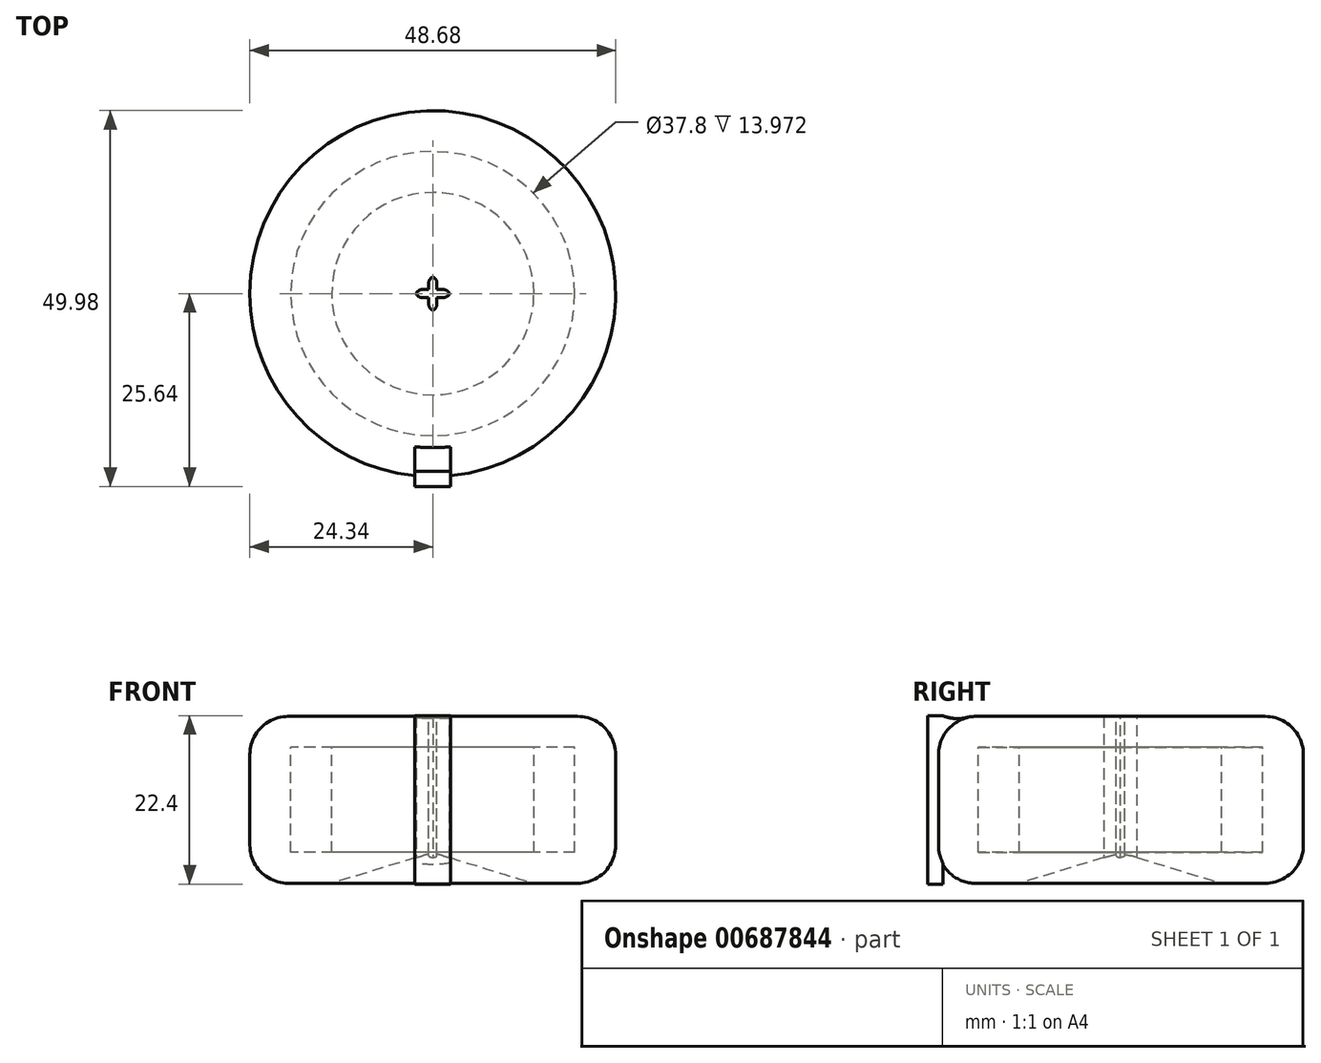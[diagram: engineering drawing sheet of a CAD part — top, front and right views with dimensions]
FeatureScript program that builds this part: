
annotation { "Feature Type Name" : "Feature", "Feature Type Description" : "" }
export const myFeature = defineFeature(function(context is Context, id is Id, definition is map)
    precondition{}
    {
        {
            var Q0;
            Q0=qCreatedBy(makeId("Front.planeOp"),FACE);
            var sketch = newSketch(context, id + "F0", { "sketchPlane" : qUnion([Q0])});
            skLineSegment(sketch, "E0.bottom", {"start": v(0, -6.99) * mm, "end": v(-18.9, -6.99) * mm});
            skLineSegment(sketch, "E0.top", {"start": v(0, 6.99) * mm, "end": v(-18.9, 6.99) * mm});
            skLineSegment(sketch, "E0.right", {"start": v(-18.9, -6.99) * mm, "end": v(-18.9, 6.99) * mm});
            skPoint(sketch, "E0.middle", {"position": v(0, 0) * mm});
            skLineSegment(sketch, "E1", {"start": v(0, 6.99) * mm, "end": v(0, -6.99) * mm});
            skPoint(sketch, "E0.left.end.orphan", {"position": v(18.9, 6.99) * mm});
            skPoint(sketch, "E2.orphan", {"position": v(18.9, -6.99) * mm});
            skLineSegment(sketch, "E3.bottom", {"start": v(-13.46, -11.1) * mm, "end": v(-24.34, -11.1) * mm});
            skLineSegment(sketch, "E3.top", {"start": v(-13.46, 11.1) * mm, "end": v(-24.34, 11.1) * mm});
            skLineSegment(sketch, "E3.left", {"start": v(-13.46, -11.1) * mm, "end": v(-13.46, 11.1) * mm});
            skLineSegment(sketch, "E3.right", {"start": v(-24.34, -11.1) * mm, "end": v(-24.34, 11.1) * mm});
            skPoint(sketch, "E3.middle", {"position": v(-18.9, 0) * mm});
            skLineSegment(sketch, "E4", {"start": v(0, -6.99) * mm, "end": v(-13.46, -11.1) * mm});
            skLineSegment(sketch, "E5", {"start": v(-13.46, 11.1) * mm, "end": v(0, 11.1) * mm});
            skLineSegment(sketch, "E6", {"start": v(0, 11.1) * mm, "end": v(0, 6.99) * mm});
            skSolve(sketch);
        }
        {
            var Q0;
            Q0 = qSketchRegion(id + "F0", true);
            var Q1;
            Q1=sQuery(id+"F0.wireOp",EDGE,"E1");
            revolve(context, id + "F1", {"entities" : qUnion([Q0]), "axis" : qUnion([Q1]), "revolveType" : RevolveType.FULL});
        }
        {
            var Q0;
            Q0=makeQuery(id+"F1.opRevolve","SWEPT_EDGE",EDGE,{"disambiguationData":[OSD([sQuery(id+"F0.wireOp",EDGE,"E3.top"),sQuery(id+"F0.wireOp",EDGE,"E3.right")])]});
            var Q1;
            Q1=makeQuery(id+"F1.opRevolve","SWEPT_EDGE",EDGE,{"disambiguationData":[OSD([sQuery(id+"F0.wireOp",EDGE,"E3.bottom"),sQuery(id+"F0.wireOp",EDGE,"E3.right")])]});
            fillet(context, id + "F2", {"entities" : qUnion([Q0, Q1]), "radius" : 5.08 * mm, "tangentPropagation" : true, "allowEdgeOverflow" : false});
        }
        {
            var Q0;
            Q0=qCreatedBy(makeId("Front.planeOp"),FACE);
            cPlane(context, id + "F3", {"entities" : qUnion([Q0]), "cplaneType" : CPlaneType.OFFSET, "offset" : 24.64 * mm, "width" : 152.4 * mm, "height" : 152.4 * mm});
        }
        {
            var Q0;
            Q0=qCreatedBy(id+"F3.planeOp",FACE);
            var sketch = newSketch(context, id + "F4", { "sketchPlane" : qUnion([Q0])});
            skLineSegment(sketch, "E7.bottom", {"start": v(2.38, -11.2) * mm, "end": v(-2.38, -11.2) * mm});
            skLineSegment(sketch, "E7.top", {"start": v(2.38, 11.2) * mm, "end": v(-2.38, 11.2) * mm});
            skLineSegment(sketch, "E7.left", {"start": v(2.38, -11.2) * mm, "end": v(2.38, 11.2) * mm});
            skLineSegment(sketch, "E7.right", {"start": v(-2.38, -11.2) * mm, "end": v(-2.38, 11.2) * mm});
            skPoint(sketch, "E7.middle", {"position": v(0, 0) * mm});
            skSolve(sketch);
        }
        {
            var Q0;
            Q0 = qSketchRegion(id + "F4", true);
            extrude(context, id + "F5", {"entities" : qUnion([Q0]), "operationType" : NewBodyOperationType.ADD, "endBound" : BoundingType.SYMMETRIC, "depth" : 2 * mm, "offsetDistance" : 25.4 * mm});
        }
        {
            var Q0;
            Q0=qCreatedBy(makeId("Top.planeOp"),FACE);
            cPlane(context, id + "F6", {"entities" : qUnion([Q0]), "cplaneType" : CPlaneType.OFFSET, "offset" : 11.68 * mm, "width" : 152.4 * mm, "height" : 152.4 * mm});
        }
        {
            var Q0;
            Q0=qCreatedBy(id+"F6.planeOp",FACE);
            var sketch = newSketch(context, id + "F7", { "sketchPlane" : qUnion([Q0])});
            skLineSegment(sketch, "E8.bottom", {"start": v(0.55, -2.34) * mm, "end": v(-0.55, -2.34) * mm});
            skLineSegment(sketch, "E8.top", {"start": v(0.55, 2.34) * mm, "end": v(-0.55, 2.34) * mm});
            skLineSegment(sketch, "E8.left", {"start": v(0.55, -2.34) * mm, "end": v(0.55, 2.34) * mm});
            skLineSegment(sketch, "E8.right", {"start": v(-0.55, -2.34) * mm, "end": v(-0.55, 2.34) * mm});
            skPoint(sketch, "E8.middle", {"position": v(0, 0) * mm});
            skLineSegment(sketch, "E9.bottom", {"start": v(2.34, -0.55) * mm, "end": v(-2.34, -0.55) * mm});
            skLineSegment(sketch, "E9.top", {"start": v(2.34, 0.55) * mm, "end": v(-2.34, 0.55) * mm});
            skLineSegment(sketch, "E9.left", {"start": v(2.34, -0.55) * mm, "end": v(2.34, 0.55) * mm});
            skLineSegment(sketch, "E9.right", {"start": v(-2.34, -0.55) * mm, "end": v(-2.34, 0.55) * mm});
            skSolve(sketch);
        }
        {
            var Q0;
            Q0 = qSketchRegion(id + "F7", true);
            extrude(context, id + "F8", {"entities" : qUnion([Q0]), "operationType" : NewBodyOperationType.REMOVE, "oppositeDirection" : true, "depth" : 25.4 * mm, "offsetDistance" : 25.4 * mm});
        }
        {
            var Q0;
            Q0=makeQuery(id+"F8.boolean.opBoolean","COPY",EDGE,{"derivedFrom":makeQuery(id+"F8.opExtrude","SWEPT_EDGE",EDGE,{"disambiguationData":[OSD([sQuery(id+"F7.wireOp",EDGE,"E9.bottom"),sQuery(id+"F7.wireOp",EDGE,"E9.right")])]})});
            var Q1;
            Q1=makeQuery(id+"F8.boolean.opBoolean","COPY",EDGE,{"derivedFrom":makeQuery(id+"F8.opExtrude","SWEPT_EDGE",EDGE,{"disambiguationData":[OSD([sQuery(id+"F7.wireOp",EDGE,"E9.top"),sQuery(id+"F7.wireOp",EDGE,"E9.right")])]})});
            var Q2;
            Q2=makeQuery(id+"F8.boolean.opBoolean","COPY",EDGE,{"derivedFrom":makeQuery(id+"F8.opExtrude","SWEPT_EDGE",EDGE,{"disambiguationData":[OSD([sQuery(id+"F7.wireOp",EDGE,"E8.top"),sQuery(id+"F7.wireOp",EDGE,"E8.right")])]})});
            var Q3;
            Q3=makeQuery(id+"F8.boolean.opBoolean","COPY",EDGE,{"derivedFrom":makeQuery(id+"F8.opExtrude","SWEPT_EDGE",EDGE,{"disambiguationData":[OSD([sQuery(id+"F7.wireOp",EDGE,"E8.top"),sQuery(id+"F7.wireOp",EDGE,"E8.left")])]})});
            var Q4;
            Q4=makeQuery(id+"F8.boolean.opBoolean","COPY",EDGE,{"derivedFrom":makeQuery(id+"F8.opExtrude","SWEPT_EDGE",EDGE,{"disambiguationData":[OSD([sQuery(id+"F7.wireOp",EDGE,"E8.bottom"),sQuery(id+"F7.wireOp",EDGE,"E8.right")])]})});
            var Q5;
            Q5=makeQuery(id+"F8.boolean.opBoolean","COPY",EDGE,{"derivedFrom":makeQuery(id+"F8.opExtrude","SWEPT_EDGE",EDGE,{"disambiguationData":[OSD([sQuery(id+"F7.wireOp",EDGE,"E8.bottom"),sQuery(id+"F7.wireOp",EDGE,"E8.left")])]})});
            var Q6;
            Q6=makeQuery(id+"F8.boolean.opBoolean","COPY",EDGE,{"derivedFrom":makeQuery(id+"F8.opExtrude","SWEPT_EDGE",EDGE,{"disambiguationData":[OSD([sQuery(id+"F7.wireOp",EDGE,"E9.bottom"),sQuery(id+"F7.wireOp",EDGE,"E9.left")])]})});
            var Q7;
            Q7=makeQuery(id+"F8.boolean.opBoolean","COPY",EDGE,{"derivedFrom":makeQuery(id+"F8.opExtrude","SWEPT_EDGE",EDGE,{"disambiguationData":[OSD([sQuery(id+"F7.wireOp",EDGE,"E9.top"),sQuery(id+"F7.wireOp",EDGE,"E9.left")])]})});
            fillet(context, id + "F9", {"entities" : qUnion([Q0, Q1, Q2, Q3, Q4, Q5, Q6, Q7]), "radius" : 1 * mm, "tangentPropagation" : true, "allowEdgeOverflow" : false});
        }
        {
            var Q0;
            Q0=makeQuery(id+"FWEGzIRy7pSOTiT_1.2.F5.boolean.opBoolean","INTERSECT",EDGE,{"derivedFrom":[makeQuery(id+"F2.opFillet","BLEND_FACE",FACE,{"disambiguationData":[OSD([sQuery(id+"F0.wireOp",EDGE,"E3.top"),sQuery(id+"F0.wireOp",EDGE,"E3.right")])]}),makeQuery(id+"FWEGzIRy7pSOTiT_1.2.F5.opExtrude","CAP_FACE",FACE,{"disambiguationData":[OSD([sQuery(id+"F4.wireOp",EDGE,"E7.bottom"),sQuery(id+"F4.wireOp",EDGE,"E7.top"),sQuery(id+"F4.wireOp",EDGE,"E7.left"),sQuery(id+"F4.wireOp",EDGE,"E7.right")])],"isStart":true})]});
            var Q1;
            Q1=makeQuery(id+"FWEGzIRy7pSOTiT_1.1.F5.boolean.opBoolean","INTERSECT",EDGE,{"derivedFrom":[makeQuery(id+"F2.opFillet","BLEND_FACE",FACE,{"disambiguationData":[OSD([sQuery(id+"F0.wireOp",EDGE,"E3.top"),sQuery(id+"F0.wireOp",EDGE,"E3.right")])]}),makeQuery(id+"FWEGzIRy7pSOTiT_1.1.F5.opExtrude","CAP_FACE",FACE,{"disambiguationData":[OSD([sQuery(id+"F4.wireOp",EDGE,"E7.bottom"),sQuery(id+"F4.wireOp",EDGE,"E7.top"),sQuery(id+"F4.wireOp",EDGE,"E7.left"),sQuery(id+"F4.wireOp",EDGE,"E7.right")])],"isStart":true})]});
            var Q2;
            Q2=makeQuery(id+"F5.boolean.opBoolean","INTERSECT",EDGE,{"derivedFrom":[makeQuery(id+"F2.opFillet","BLEND_FACE",FACE,{"disambiguationData":[OSD([sQuery(id+"F0.wireOp",EDGE,"E3.top"),sQuery(id+"F0.wireOp",EDGE,"E3.right")])]}),makeQuery(id+"F5.opExtrude","CAP_FACE",FACE,{"disambiguationData":[OSD([sQuery(id+"F4.wireOp",EDGE,"E7.bottom"),sQuery(id+"F4.wireOp",EDGE,"E7.top"),sQuery(id+"F4.wireOp",EDGE,"E7.left"),sQuery(id+"F4.wireOp",EDGE,"E7.right")])],"isStart":true})]});
            var Q3;
            Q3=makeQuery(id+"FWEGzIRy7pSOTiT_1.3.F5.boolean.opBoolean","INTERSECT",EDGE,{"derivedFrom":[makeQuery(id+"F2.opFillet","BLEND_FACE",FACE,{"disambiguationData":[OSD([sQuery(id+"F0.wireOp",EDGE,"E3.top"),sQuery(id+"F0.wireOp",EDGE,"E3.right")])]}),makeQuery(id+"FWEGzIRy7pSOTiT_1.3.F5.opExtrude","CAP_FACE",FACE,{"disambiguationData":[OSD([sQuery(id+"F4.wireOp",EDGE,"E7.bottom"),sQuery(id+"F4.wireOp",EDGE,"E7.top"),sQuery(id+"F4.wireOp",EDGE,"E7.left"),sQuery(id+"F4.wireOp",EDGE,"E7.right")])],"isStart":true})]});
            var Q4;
            Q4=makeQuery(id+"FWEGzIRy7pSOTiT_1.9.F5.boolean.opBoolean","INTERSECT",EDGE,{"derivedFrom":[makeQuery(id+"F2.opFillet","BLEND_FACE",FACE,{"disambiguationData":[OSD([sQuery(id+"F0.wireOp",EDGE,"E3.top"),sQuery(id+"F0.wireOp",EDGE,"E3.right")])]}),makeQuery(id+"FWEGzIRy7pSOTiT_1.9.F5.opExtrude","CAP_FACE",FACE,{"disambiguationData":[OSD([sQuery(id+"F4.wireOp",EDGE,"E7.bottom"),sQuery(id+"F4.wireOp",EDGE,"E7.top"),sQuery(id+"F4.wireOp",EDGE,"E7.left"),sQuery(id+"F4.wireOp",EDGE,"E7.right")])],"isStart":true})]});
            var Q5;
            Q5=makeQuery(id+"FWEGzIRy7pSOTiT_1.8.F5.boolean.opBoolean","INTERSECT",EDGE,{"derivedFrom":[makeQuery(id+"F2.opFillet","BLEND_FACE",FACE,{"disambiguationData":[OSD([sQuery(id+"F0.wireOp",EDGE,"E3.top"),sQuery(id+"F0.wireOp",EDGE,"E3.right")])]}),makeQuery(id+"FWEGzIRy7pSOTiT_1.8.F5.opExtrude","CAP_FACE",FACE,{"disambiguationData":[OSD([sQuery(id+"F4.wireOp",EDGE,"E7.bottom"),sQuery(id+"F4.wireOp",EDGE,"E7.top"),sQuery(id+"F4.wireOp",EDGE,"E7.left"),sQuery(id+"F4.wireOp",EDGE,"E7.right")])],"isStart":true})]});
            var Q6;
            Q6=makeQuery(id+"FWEGzIRy7pSOTiT_1.7.F5.boolean.opBoolean","INTERSECT",EDGE,{"derivedFrom":[makeQuery(id+"F2.opFillet","BLEND_FACE",FACE,{"disambiguationData":[OSD([sQuery(id+"F0.wireOp",EDGE,"E3.top"),sQuery(id+"F0.wireOp",EDGE,"E3.right")])]}),makeQuery(id+"FWEGzIRy7pSOTiT_1.7.F5.opExtrude","CAP_FACE",FACE,{"disambiguationData":[OSD([sQuery(id+"F4.wireOp",EDGE,"E7.bottom"),sQuery(id+"F4.wireOp",EDGE,"E7.top"),sQuery(id+"F4.wireOp",EDGE,"E7.left"),sQuery(id+"F4.wireOp",EDGE,"E7.right")])],"isStart":true})]});
            var Q7;
            Q7=makeQuery(id+"FWEGzIRy7pSOTiT_1.6.F5.boolean.opBoolean","INTERSECT",EDGE,{"derivedFrom":[makeQuery(id+"F2.opFillet","BLEND_FACE",FACE,{"disambiguationData":[OSD([sQuery(id+"F0.wireOp",EDGE,"E3.top"),sQuery(id+"F0.wireOp",EDGE,"E3.right")])]}),makeQuery(id+"FWEGzIRy7pSOTiT_1.6.F5.opExtrude","CAP_FACE",FACE,{"disambiguationData":[OSD([sQuery(id+"F4.wireOp",EDGE,"E7.bottom"),sQuery(id+"F4.wireOp",EDGE,"E7.top"),sQuery(id+"F4.wireOp",EDGE,"E7.left"),sQuery(id+"F4.wireOp",EDGE,"E7.right")])],"isStart":true})]});
            var Q8;
            Q8=makeQuery(id+"FWEGzIRy7pSOTiT_1.5.F5.boolean.opBoolean","INTERSECT",EDGE,{"derivedFrom":[makeQuery(id+"F2.opFillet","BLEND_FACE",FACE,{"disambiguationData":[OSD([sQuery(id+"F0.wireOp",EDGE,"E3.top"),sQuery(id+"F0.wireOp",EDGE,"E3.right")])]}),makeQuery(id+"FWEGzIRy7pSOTiT_1.5.F5.opExtrude","CAP_FACE",FACE,{"disambiguationData":[OSD([sQuery(id+"F4.wireOp",EDGE,"E7.bottom"),sQuery(id+"F4.wireOp",EDGE,"E7.top"),sQuery(id+"F4.wireOp",EDGE,"E7.left"),sQuery(id+"F4.wireOp",EDGE,"E7.right")])],"isStart":true})]});
            var Q9;
            Q9=makeQuery(id+"FWEGzIRy7pSOTiT_1.4.F5.boolean.opBoolean","INTERSECT",EDGE,{"derivedFrom":[makeQuery(id+"F2.opFillet","BLEND_FACE",FACE,{"disambiguationData":[OSD([sQuery(id+"F0.wireOp",EDGE,"E3.top"),sQuery(id+"F0.wireOp",EDGE,"E3.right")])]}),makeQuery(id+"FWEGzIRy7pSOTiT_1.4.F5.opExtrude","CAP_FACE",FACE,{"disambiguationData":[OSD([sQuery(id+"F4.wireOp",EDGE,"E7.bottom"),sQuery(id+"F4.wireOp",EDGE,"E7.top"),sQuery(id+"F4.wireOp",EDGE,"E7.left"),sQuery(id+"F4.wireOp",EDGE,"E7.right")])],"isStart":true})]});
            var Q10;
            Q10=makeQuery(id+"FWEGzIRy7pSOTiT_1.3.F5.boolean.opBoolean","INTERSECT",EDGE,{"derivedFrom":[makeQuery(id+"F2.opFillet","BLEND_FACE",FACE,{"disambiguationData":[OSD([sQuery(id+"F0.wireOp",EDGE,"E3.bottom"),sQuery(id+"F0.wireOp",EDGE,"E3.right")])]}),makeQuery(id+"FWEGzIRy7pSOTiT_1.3.F5.opExtrude","CAP_FACE",FACE,{"disambiguationData":[OSD([sQuery(id+"F4.wireOp",EDGE,"E7.bottom"),sQuery(id+"F4.wireOp",EDGE,"E7.top"),sQuery(id+"F4.wireOp",EDGE,"E7.left"),sQuery(id+"F4.wireOp",EDGE,"E7.right")])],"isStart":true})]});
            var Q11;
            Q11=makeQuery(id+"FWEGzIRy7pSOTiT_1.2.F5.boolean.opBoolean","INTERSECT",EDGE,{"derivedFrom":[makeQuery(id+"F2.opFillet","BLEND_FACE",FACE,{"disambiguationData":[OSD([sQuery(id+"F0.wireOp",EDGE,"E3.bottom"),sQuery(id+"F0.wireOp",EDGE,"E3.right")])]}),makeQuery(id+"FWEGzIRy7pSOTiT_1.2.F5.opExtrude","CAP_FACE",FACE,{"disambiguationData":[OSD([sQuery(id+"F4.wireOp",EDGE,"E7.bottom"),sQuery(id+"F4.wireOp",EDGE,"E7.top"),sQuery(id+"F4.wireOp",EDGE,"E7.left"),sQuery(id+"F4.wireOp",EDGE,"E7.right")])],"isStart":true})]});
            var Q12;
            Q12=makeQuery(id+"FWEGzIRy7pSOTiT_1.1.F5.boolean.opBoolean","INTERSECT",EDGE,{"derivedFrom":[makeQuery(id+"F2.opFillet","BLEND_FACE",FACE,{"disambiguationData":[OSD([sQuery(id+"F0.wireOp",EDGE,"E3.bottom"),sQuery(id+"F0.wireOp",EDGE,"E3.right")])]}),makeQuery(id+"FWEGzIRy7pSOTiT_1.1.F5.opExtrude","CAP_FACE",FACE,{"disambiguationData":[OSD([sQuery(id+"F4.wireOp",EDGE,"E7.bottom"),sQuery(id+"F4.wireOp",EDGE,"E7.top"),sQuery(id+"F4.wireOp",EDGE,"E7.left"),sQuery(id+"F4.wireOp",EDGE,"E7.right")])],"isStart":true})]});
            var Q13;
            Q13=makeQuery(id+"FWEGzIRy7pSOTiT_1.4.F5.boolean.opBoolean","INTERSECT",EDGE,{"derivedFrom":[makeQuery(id+"F2.opFillet","BLEND_FACE",FACE,{"disambiguationData":[OSD([sQuery(id+"F0.wireOp",EDGE,"E3.bottom"),sQuery(id+"F0.wireOp",EDGE,"E3.right")])]}),makeQuery(id+"FWEGzIRy7pSOTiT_1.4.F5.opExtrude","CAP_FACE",FACE,{"disambiguationData":[OSD([sQuery(id+"F4.wireOp",EDGE,"E7.bottom"),sQuery(id+"F4.wireOp",EDGE,"E7.top"),sQuery(id+"F4.wireOp",EDGE,"E7.left"),sQuery(id+"F4.wireOp",EDGE,"E7.right")])],"isStart":true})]});
            var Q14;
            Q14=makeQuery(id+"FWEGzIRy7pSOTiT_1.9.F5.boolean.opBoolean","INTERSECT",EDGE,{"derivedFrom":[makeQuery(id+"F2.opFillet","BLEND_FACE",FACE,{"disambiguationData":[OSD([sQuery(id+"F0.wireOp",EDGE,"E3.bottom"),sQuery(id+"F0.wireOp",EDGE,"E3.right")])]}),makeQuery(id+"FWEGzIRy7pSOTiT_1.9.F5.opExtrude","CAP_FACE",FACE,{"disambiguationData":[OSD([sQuery(id+"F4.wireOp",EDGE,"E7.bottom"),sQuery(id+"F4.wireOp",EDGE,"E7.top"),sQuery(id+"F4.wireOp",EDGE,"E7.left"),sQuery(id+"F4.wireOp",EDGE,"E7.right")])],"isStart":true})]});
            var Q15;
            Q15=makeQuery(id+"FWEGzIRy7pSOTiT_1.8.F5.boolean.opBoolean","INTERSECT",EDGE,{"derivedFrom":[makeQuery(id+"F2.opFillet","BLEND_FACE",FACE,{"disambiguationData":[OSD([sQuery(id+"F0.wireOp",EDGE,"E3.bottom"),sQuery(id+"F0.wireOp",EDGE,"E3.right")])]}),makeQuery(id+"FWEGzIRy7pSOTiT_1.8.F5.opExtrude","CAP_FACE",FACE,{"disambiguationData":[OSD([sQuery(id+"F4.wireOp",EDGE,"E7.bottom"),sQuery(id+"F4.wireOp",EDGE,"E7.top"),sQuery(id+"F4.wireOp",EDGE,"E7.left"),sQuery(id+"F4.wireOp",EDGE,"E7.right")])],"isStart":true})]});
            var Q16;
            Q16=makeQuery(id+"FWEGzIRy7pSOTiT_1.7.F5.boolean.opBoolean","INTERSECT",EDGE,{"derivedFrom":[makeQuery(id+"F2.opFillet","BLEND_FACE",FACE,{"disambiguationData":[OSD([sQuery(id+"F0.wireOp",EDGE,"E3.bottom"),sQuery(id+"F0.wireOp",EDGE,"E3.right")])]}),makeQuery(id+"FWEGzIRy7pSOTiT_1.7.F5.opExtrude","CAP_FACE",FACE,{"disambiguationData":[OSD([sQuery(id+"F4.wireOp",EDGE,"E7.bottom"),sQuery(id+"F4.wireOp",EDGE,"E7.top"),sQuery(id+"F4.wireOp",EDGE,"E7.left"),sQuery(id+"F4.wireOp",EDGE,"E7.right")])],"isStart":true})]});
            var Q17;
            Q17=makeQuery(id+"FWEGzIRy7pSOTiT_1.6.F5.boolean.opBoolean","INTERSECT",EDGE,{"derivedFrom":[makeQuery(id+"F2.opFillet","BLEND_FACE",FACE,{"disambiguationData":[OSD([sQuery(id+"F0.wireOp",EDGE,"E3.bottom"),sQuery(id+"F0.wireOp",EDGE,"E3.right")])]}),makeQuery(id+"FWEGzIRy7pSOTiT_1.6.F5.opExtrude","CAP_FACE",FACE,{"disambiguationData":[OSD([sQuery(id+"F4.wireOp",EDGE,"E7.bottom"),sQuery(id+"F4.wireOp",EDGE,"E7.top"),sQuery(id+"F4.wireOp",EDGE,"E7.left"),sQuery(id+"F4.wireOp",EDGE,"E7.right")])],"isStart":true})]});
            var Q18;
            Q18=makeQuery(id+"FWEGzIRy7pSOTiT_1.5.F5.boolean.opBoolean","INTERSECT",EDGE,{"derivedFrom":[makeQuery(id+"F2.opFillet","BLEND_FACE",FACE,{"disambiguationData":[OSD([sQuery(id+"F0.wireOp",EDGE,"E3.bottom"),sQuery(id+"F0.wireOp",EDGE,"E3.right")])]}),makeQuery(id+"FWEGzIRy7pSOTiT_1.5.F5.opExtrude","CAP_FACE",FACE,{"disambiguationData":[OSD([sQuery(id+"F4.wireOp",EDGE,"E7.bottom"),sQuery(id+"F4.wireOp",EDGE,"E7.top"),sQuery(id+"F4.wireOp",EDGE,"E7.left"),sQuery(id+"F4.wireOp",EDGE,"E7.right")])],"isStart":true})]});
            fillet(context, id + "F10", {"entities" : qUnion([Q0, Q1, Q2, Q3, Q4, Q5, Q6, Q7, Q8, Q9, Q10, Q11, Q12, Q13, Q14, Q15, Q16, Q17, Q18]), "radius" : 5.08 * mm, "tangentPropagation" : true, "allowEdgeOverflow" : false});
        }
    });
